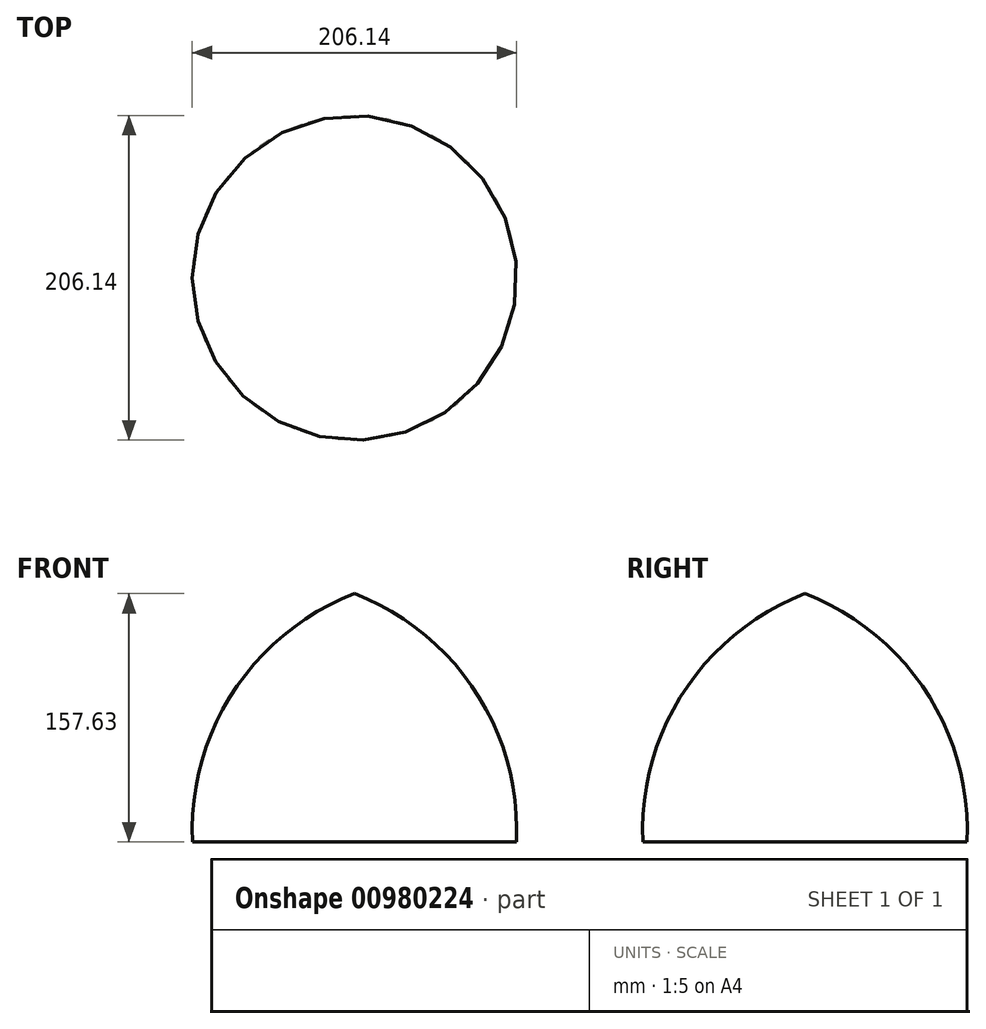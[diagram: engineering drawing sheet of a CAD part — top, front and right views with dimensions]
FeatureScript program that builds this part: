
annotation { "Feature Type Name" : "Feature", "Feature Type Description" : "" }
export const myFeature = defineFeature(function(context is Context, id is Id, definition is map)
    precondition{}
    {
        {
            var Q0;
            Q0=qCreatedBy(makeId("Front.planeOp"),FACE);
            var sketch = newSketch(context, id + "F0", { "sketchPlane" : qUnion([Q0])});
            skLineSegment(sketch, "E0", {"start": v(0, -114.61) * mm, "end": v(0, 140.32) * mm});
            skLineSegment(sketch, "E1", {"start": v(0, 90.17) * mm, "end": v(151.64, 90.17) * mm});
            skSolve(sketch);
        }
        {
            var Q0;
            Q0=qCreatedBy(makeId("Front.planeOp"),FACE);
            var sketch = newSketch(context, id + "F1", { "sketchPlane" : qUnion([Q0])});
            skArc(sketch, "E2", {"start": v(0, 79.44) * mm, "mid": v(-76.91, 17.25) * mm, "end": v(-102.9, -78.19) * mm});
            skSolve(sketch);
        }
        {
            var Q0;
            Q0=sQuery(id+"F1.wireOp",EDGE,"E2");
            var Q1;
            Q1=sQuery(id+"F0.wireOp",EDGE,"E0");
            revolve(context, id + "F2", {"bodyType" : ToolBodyType.SURFACE, "surfaceOperationType" : NewSurfaceOperationType.NEW, "surfaceEntities" : qUnion([Q0]), "axis" : qUnion([Q1]), "revolveType" : RevolveType.FULL});
        }
    });
